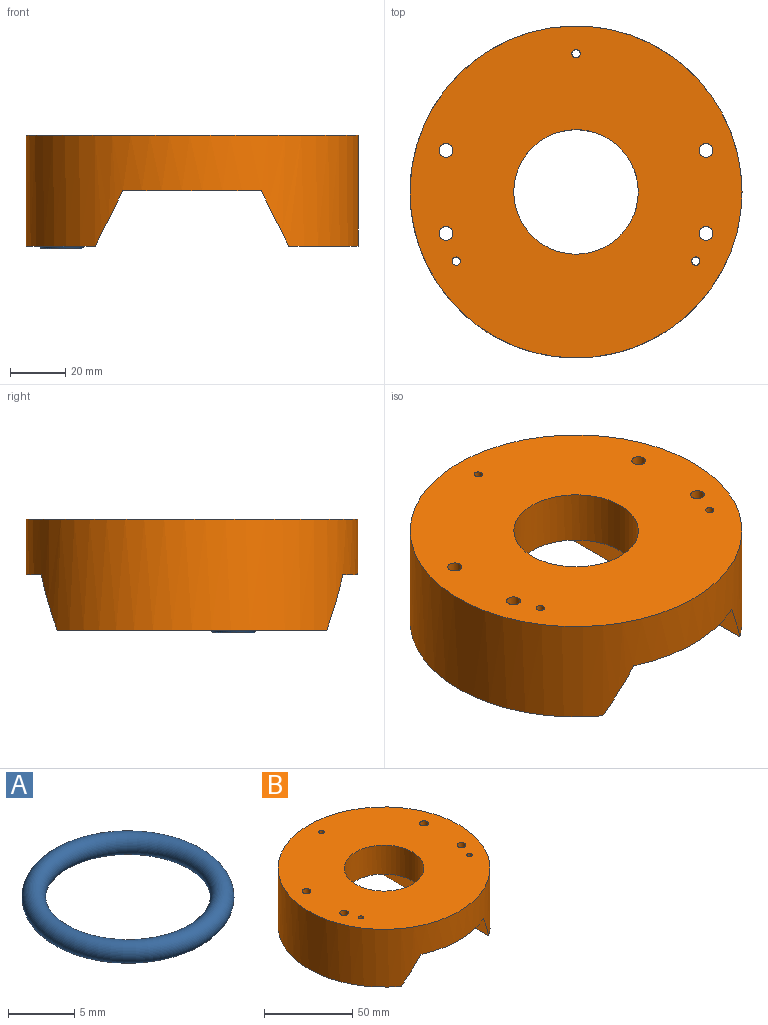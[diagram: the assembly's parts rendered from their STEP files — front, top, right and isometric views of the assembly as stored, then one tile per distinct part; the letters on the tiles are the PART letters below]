
ASSEMBLY  parts=2 mates=1
PART A: 1 faces, bbox 17.3x17.3x1.8 mm
  f0: torus R=7.1mm, axis (0,0,-1), area 249.5mm2
PART B: 31 faces, bbox 120x120x40 mm
  f0: plane 12.2x12.2mm, normal (0,0,-1), area 97.3mm2, adj f18,f28
  f1: plane 12.2x12.2mm, normal (0,0,-1), area 97.3mm2, adj f17,f25
  f2: plane 12.2x12.2mm, normal (0,0,-1), area 97.3mm2, adj f15,f22
  f3: plane 12.2x12.2mm, normal (0,0,-1), area 97.3mm2, adj f16,f19
  f4: cylinder r=60mm len=120mm, axis (0,0,-1), area 12562.1mm2, adj f5,f6,f7,f8,f9,f10
  f5: plane 97.47x25mm, normal (0,0,-1), area 1287.7mm2, adj f4,f10,f14,f26,f29
  f6: plane 120x120mm, normal (0,0,1), area 9619.6mm2, adj f4,f11,f12,f13,f14,f15,f16,f17
  f7: plane 97.47x25mm, normal (0,0,-1), area 1287.7mm2, adj f4,f9,f13,f20,f23
  f8: plane 120x50mm, normal (0,0,-1), area 4224.1mm2, adj f4,f9,f10,f11,f12
  f9: plane 109.09x20mm, normal (0.89,0,-0.45), area 2319mm2, adj f4,f7,f8
  f10: plane 109.09x20mm, normal (-0.89,0,-0.45), area 2319mm2, adj f4,f5,f8
  f11: cylinder r=22.5mm len=45mm, axis (0,0,1), area 2827.4mm2, adj f6,f8
  f12: cylinder r=1.5mm len=20mm, axis (0,0,1), area 188.5mm2, adj f6,f8
  f13: cylinder r=1.5mm len=40mm, axis (0,0,1), area 377mm2, adj f6,f7
  f14: cylinder r=1.5mm len=40mm, axis (0,0,1), area 377mm2, adj f5,f6
  f15: cylinder r=2.5mm len=40mm, axis (0,0,-1), area 628.3mm2, adj f2,f6
  f16: cylinder r=2.5mm len=40mm, axis (0,0,-1), area 628.3mm2, adj f3,f6
  f17: cylinder r=2.5mm len=40mm, axis (0,0,-1), area 628.3mm2, adj f1,f6
  f18: cylinder r=2.5mm len=40mm, axis (0,0,-1), area 628.3mm2, adj f0,f6
  f19: cylinder r=6.1mm len=12.2mm, axis (0,0,-1), area 38.3mm2, adj f3,f21
  f20: cylinder r=8.1mm len=16.2mm, axis (0,0,-1), area 50.9mm2, adj f7,f21
  f21: plane 16.2x16.2mm, normal (0,0,-1), area 89.2mm2, adj f19,f20
  f22: cylinder r=6.1mm len=12.2mm, axis (0,0,-1), area 38.3mm2, adj f2,f24
  f23: cylinder r=8.1mm len=16.2mm, axis (0,0,-1), area 50.9mm2, adj f7,f24
  f24: plane 16.2x16.2mm, normal (0,0,-1), area 89.2mm2, adj f22,f23
  f25: cylinder r=6.1mm len=12.2mm, axis (0,0,-1), area 38.3mm2, adj f1,f27
  f26: cylinder r=8.1mm len=16.2mm, axis (0,0,-1), area 50.9mm2, adj f5,f27
  f27: plane 16.2x16.2mm, normal (0,0,-1), area 89.2mm2, adj f25,f26
  f28: cylinder r=6.1mm len=12.2mm, axis (0,0,-1), area 38.3mm2, adj f0,f30
  f29: cylinder r=8.1mm len=16.2mm, axis (0,0,-1), area 50.9mm2, adj f5,f30
  f30: plane 16.2x16.2mm, normal (0,0,-1), area 89.2mm2, adj f28,f29
PLACE A t=(-150.97,-51.41,10.04)mm
PLACE B t=(-103.97,-36.41,10.04)mm
MATE fastened B.f15 <-> A.f0  axis (0,0,-1) through (-150.97,-51.41,10.04)mm
